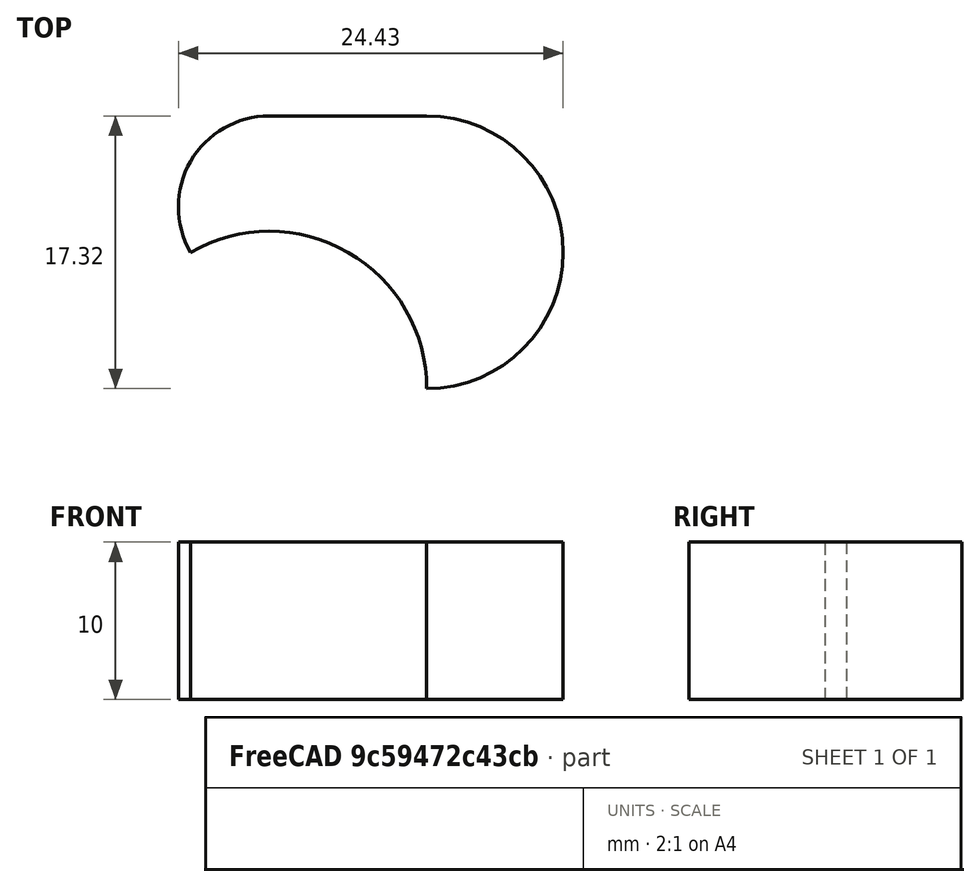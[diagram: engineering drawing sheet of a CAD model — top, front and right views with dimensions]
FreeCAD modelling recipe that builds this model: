
FCSTD DOCUMENT  (FreeCAD 0.17R9822 (Git))
Label: CCW Comp Error
License: All rights reserved
LicenseURL: http://en.wikipedia.org/wiki/All_rights_reserved
objects: Path::FeaturePython×2, Sketcher::SketchObject×1, PartDesign::Pad×1, PartDesign::Body×1, Path::FeatureCompoundPython×1
note: 4 computed .brp shape members not serialized (recipe doc carries the construction recipe); baked Part::Feature solids carry a one-line shape summary decoded from their .brp

FEATURE [Sketcher::SketchObject] Sketch
  MapMode = 5
  Support = -> [XY_Plane]
  sketch-geometry (10):
    g0: LineSegment [constr] StartX=5 StartY=-8.66025 StartZ=0 EndX=10 EndY=0 EndZ=0
    g1: LineSegment [constr] StartX=10 StartY=0 StartZ=0 EndX=5 EndY=8.66025 EndZ=0
    g2: LineSegment StartX=5 StartY=8.66025 StartZ=0 EndX=-5 EndY=8.66025 EndZ=0
    g3: LineSegment [constr] StartX=-5 StartY=8.66025 StartZ=0 EndX=-10 EndY=0 EndZ=0
    g4: LineSegment [constr] StartX=-10 StartY=0 StartZ=0 EndX=-5 EndY=-8.66025 EndZ=0
    g5: LineSegment [constr] StartX=-5 StartY=-8.66025 StartZ=0 EndX=5 EndY=-8.66025 EndZ=0
    g6: Circle [constr] CenterX=0 CenterY=0 CenterZ=0 NormalX=0 NormalY=0 NormalZ=1 Radius=10
    g7: ArcOfCircle CenterX=-5.00002 CenterY=2.88677 CenterZ=0 NormalX=0 NormalY=0 NormalZ=1 Radius=5.77349 StartAngle=1.57079 EndAngle=3.6652
    g8: ArcOfCircle CenterX=5 CenterY=0 CenterZ=0 NormalX=0 NormalY=0 NormalZ=1 Radius=8.66025 StartAngle=4.71239 EndAngle=7.85398
    g9: ArcOfCircle CenterX=-5 CenterY=-8.66025 CenterZ=0 NormalX=0 NormalY=0 NormalZ=1 Radius=10 StartAngle=0 EndAngle=2.0944
  constraints (25):
    c: Coincident(g0,g1)
    c: Coincident(g1,g2)
    c: Coincident(g2,g3)
    c: Coincident(g3,g4)
    c: Coincident(g4,g5)
    c: Coincident(g5,g0)
    c: Equal(g0, g1-g5) x5
    c: PointOnObject(g0,g6)
    c: PointOnObject(g1,g6)
    c: PointOnObject(g2,g6)
    c: PointOnObject(g3,g6)
    c: PointOnObject(g4,g6)
    c: PointOnObject(g5,g6)
    c: Horizontal(g2)
    c: Coincident(g6,g-1)
    c: DistanceX(g2,g2) = 10
    c: Coincident(g7,g3)
    c: Coincident(g7,g2)
    c: Tangent(g7,g2)
    c: Coincident(g8,g1)
    c: Coincident(g8,g0)
    c: Tangent(g2,g8)
    c: Coincident(g9,g3)
    c: Coincident(g0,g9)
    c: PointOnObject(g9,g6)
FEATURE [PartDesign::Pad] Pad
  Length = 10
  Length2 = 100
  Profile = -> Sketch
  Type = 0
FEATURE [PartDesign::Body] Body
  Group = -> [Sketch,Pad]
  Origin = -> BodyOrigin
  Tip = -> Pad
FEATURE [Path::FeaturePython] TC001  label="TC001: EM 10mm"  # Path/CAM operation (typed FeaturePython)
  HorizFeed = 0
  HorizRapid = 0
  SpindleDir = 0
  SpindleSpeed = 0
  ToolNumber = 1
  VertFeed = 0
  VertRapid = 0
FEATURE [Path::FeaturePython] Contour  label="Contour :TC001"  # Path/CAM operation (typed FeaturePython)
  Active = true
  ClearanceHeight = 15
  Direction = 0
  EndPoint = (0,0,0)
  ExtendAtEnd = 0
  ExtendAtStart = 0
  FinalDepth = 0
  LeadInLineLen = 0
  LeadOutLineLen = 0
  OffsetExtra = 0
  RollRadius = 0
  SafeHeight = 13
  Side = 0
  StartDepth = 10
  StartPoint = (0,0,0)
  StepDown = 1
  ToolDescription = TC001
  ToolNumber = 1
  UseComp = true
  UseEndPoint = false
  UseStartPoint = false
FEATURE [Path::FeatureCompoundPython] Job  # Path/CAM operation (typed FeaturePython)
  Base = -> Pad
  Group = -> [TC001,Contour]
  MachineName = LinuxCNC
  MachineUnits = 0
  OutputFile = <userpath>/Desktop/bam coveres/post test.ngc
  PostProcessor = 8
  UsePlacements = false
  X_Max = 500
  X_Min = 0
  Y_Max = 300
  Y_Min = 0
  Z_Max = 300
  Z_Min = 0
